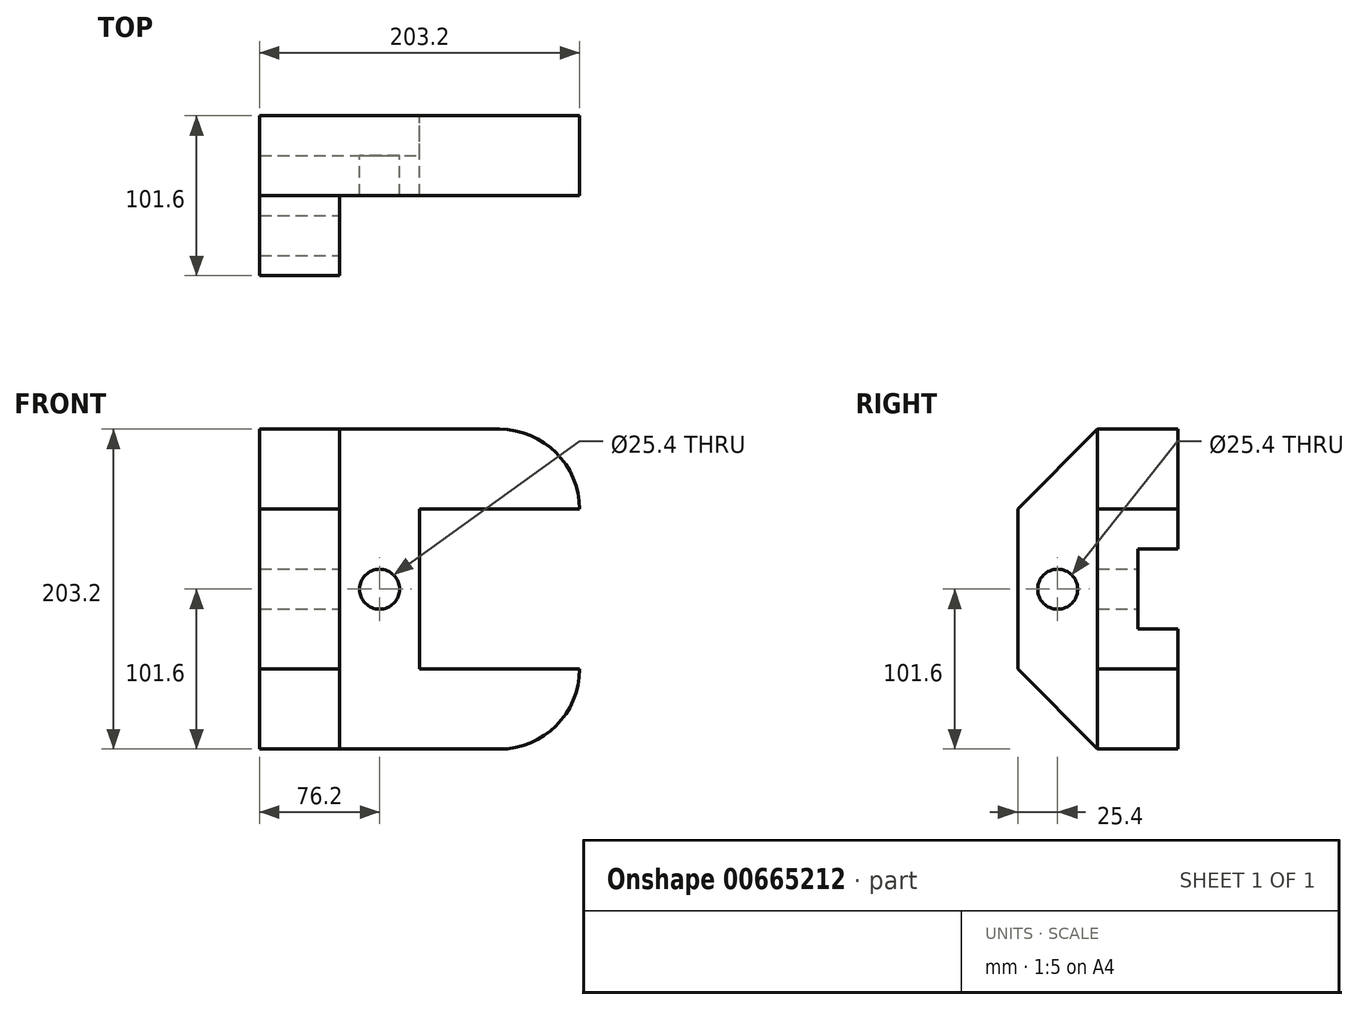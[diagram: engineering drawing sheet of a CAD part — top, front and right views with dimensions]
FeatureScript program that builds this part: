
annotation { "Feature Type Name" : "Feature", "Feature Type Description" : "" }
export const myFeature = defineFeature(function(context is Context, id is Id, definition is map)
    precondition{}
    {
        {
            var Q0;
            Q0=qCreatedBy(makeId("Front.planeOp"),FACE);
            var sketch = newSketch(context, id + "F0", { "sketchPlane" : qUnion([Q0])});
            skLineSegment(sketch, "E0", {"start": v(0, 0) * mm, "end": v(0, 203.2) * mm});
            skLineSegment(sketch, "E1", {"start": v(0, 203.2) * mm, "end": v(152.4, 203.2) * mm});
            skLineSegment(sketch, "E2", {"start": v(0, 0) * mm, "end": v(152.4, 0) * mm});
            skLineSegment(sketch, "E3", {"start": v(203.2, 50.8) * mm, "end": v(203.2, 50.8) * mm});
            skLineSegment(sketch, "E4", {"start": v(203.2, 50.8) * mm, "end": v(101.6, 50.8) * mm});
            skLineSegment(sketch, "E5", {"start": v(101.6, 50.8) * mm, "end": v(101.6, 152.4) * mm});
            skLineSegment(sketch, "E6", {"start": v(101.6, 152.4) * mm, "end": v(203.2, 152.4) * mm});
            skLineSegment(sketch, "E7", {"start": v(203.2, 152.4) * mm, "end": v(203.2, 152.4) * mm});
            skPoint(sketch, "E8.visualSharp", {"position": v(203.2, 203.2) * mm});
            skArc(sketch, "E8.filletArc", {"start": v(203.2, 152.4) * mm, "mid": v(188.32, 188.32) * mm, "end": v(152.4, 203.2) * mm});
            skPoint(sketch, "E9.visualSharp", {"position": v(203.2, 0) * mm});
            skArc(sketch, "E9.filletArc", {"start": v(152.4, 0) * mm, "mid": v(188.32, 14.88) * mm, "end": v(203.2, 50.8) * mm});
            skLineSegment(sketch, "E10.0", {"start": v(50.8, 0) * mm, "end": v(50.8, 203.2) * mm});
            skCircle(sketch, "E11", {"center": v(76.2, 101.6) * mm, "radius": 12.7 * mm});
            skPoint(sketch, "E12", {"position": v(101.6, 101.6) * mm});
            skSolve(sketch);
        }
        {
            var Q0;
            Q0=makeQuery(id+"F0.imprint","IMPRINT",FACE,{"disambiguationData":[TD([[makeQuery(id+"F0.imprint","IMPRINT",EDGE,{"derivedFrom":sQuery(id+"F0.wireOp",EDGE,"E4")}),1.0]])]});
            extrude(context, id + "F1", {"entities" : qUnion([Q0]), "depth" : 50.8 * mm, "offsetDistance" : 25.4 * mm});
        }
        {
            var Q0;
            {var subQ0=sQuery(id+"F0.wireOp",EDGE,"E0");Q0=makeQuery(id+"F0.imprint","IMPRINT",FACE,{"disambiguationData":[TD([[makeQuery(id+"F0.imprint","IMPRINT",EDGE,{"derivedFrom":subQ0}),-1.0]])]});}
            extrude(context, id + "F2", {"entities" : qUnion([Q0]), "operationType" : NewBodyOperationType.ADD, "depth" : 101.6 * mm, "offsetDistance" : 25.4 * mm});
        }
        {
            var Q0;
            Q0=makeQuery(id+"F1.opExtrude","SWEPT_FACE",FACE,{"disambiguationData":[OSD([sQuery(id+"F0.wireOp",EDGE,"E5")])]});
            var sketch = newSketch(context, id + "F3", { "sketchPlane" : qUnion([Q0])});
            skCircle(sketch, "E13", {"center": v(-76.2, 101.6) * mm, "radius": 12.7 * mm});
            skLineSegment(sketch, "E14.0", {"start": v(-101.6, 50.8) * mm, "end": v(-50.8, 50.8) * mm});
            skLineSegment(sketch, "E15.0", {"start": v(-101.6, 152.4) * mm, "end": v(-50.8, 152.4) * mm});
            skLineSegment(sketch, "E16", {"start": v(-101.6, 50.8) * mm, "end": v(-50.8, 0) * mm});
            skLineSegment(sketch, "E17", {"start": v(-50.8, 0) * mm, "end": v(-101.6, 0) * mm});
            skLineSegment(sketch, "E18", {"start": v(-101.6, 0) * mm, "end": v(-101.6, 50.8) * mm});
            skLineSegment(sketch, "E19", {"start": v(-101.6, 152.4) * mm, "end": v(-50.8, 203.2) * mm});
            skLineSegment(sketch, "E20", {"start": v(-50.8, 203.2) * mm, "end": v(-101.6, 203.2) * mm});
            skLineSegment(sketch, "E21", {"start": v(-101.6, 203.2) * mm, "end": v(-101.6, 152.4) * mm});
            skLineSegment(sketch, "E22.0", {"start": v(-25.23, 76.2) * mm, "end": v(0, 76.2) * mm});
            skLineSegment(sketch, "E23.0", {"start": v(-25.23, 127) * mm, "end": v(0, 127) * mm});
            skLineSegment(sketch, "E24", {"start": v(-25.23, 76.2) * mm, "end": v(-25.23, 127) * mm});
            skPoint(sketch, "E25.orphan", {"position": v(-50.45, 127) * mm});
            skPoint(sketch, "E26.orphan", {"position": v(-50.45, 76.2) * mm});
            skSolve(sketch);
        }
        {
            var Q0;
            Q0=makeQuery(id+"F3.imprint","IMPRINT",FACE,{"disambiguationData":[TD([[makeQuery(id+"F3.imprint","IMPRINT",EDGE,{"derivedFrom":sQuery(id+"F3.wireOp",EDGE,"E16")}),-1.0]])]});
            var Q1;
            Q1=makeQuery(id+"F3.imprint","IMPRINT",FACE,{"disambiguationData":[TD([[makeQuery(id+"F3.imprint","IMPRINT",EDGE,{"derivedFrom":sQuery(id+"F3.wireOp",EDGE,"E19")}),1.0]])]});
            var Q2;
            Q2=makeQuery(id+"F3.imprint","IMPRINT",FACE,{"disambiguationData":[TD([[makeQuery(id+"F3.imprint","IMPRINT",EDGE,{"derivedFrom":sQuery(id+"F3.wireOp",EDGE,"E13")}),1.0]])]});
            var Q3;
            {var subQ0=sQuery(id+"F3.wireOp",EDGE,"E22.0");Q3=makeQuery(id+"F3.imprint","IMPRINT",FACE,{"disambiguationData":[TD([[makeQuery(id+"F3.imprint","IMPRINT",EDGE,{"derivedFrom":subQ0}),1.0]])]});}
            extrude(context, id + "F4", {"entities" : qUnion([Q0, Q1, Q2, Q3]), "operationType" : NewBodyOperationType.REMOVE, "endBound" : BoundingType.THROUGH_ALL, "oppositeDirection" : true, "depth" : 25.4 * mm, "offsetDistance" : 25.4 * mm});
        }
    });
